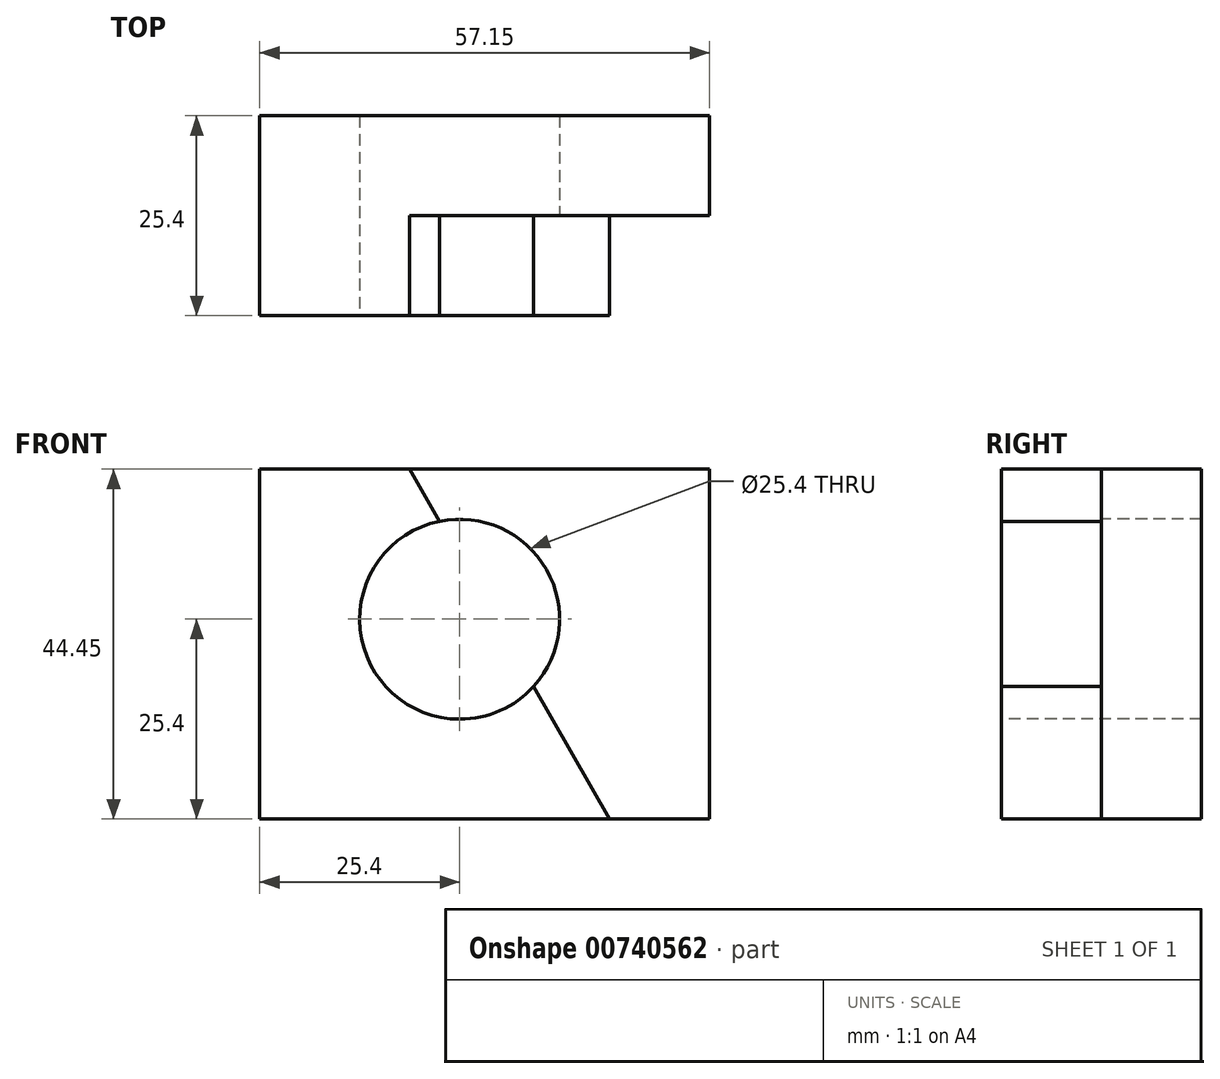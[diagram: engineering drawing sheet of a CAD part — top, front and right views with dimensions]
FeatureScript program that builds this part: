
annotation { "Feature Type Name" : "Feature", "Feature Type Description" : "" }
export const myFeature = defineFeature(function(context is Context, id is Id, definition is map)
    precondition{}
    {
        {
            var Q0;
            Q0=qCreatedBy(makeId("Front.planeOp"),FACE);
            var sketch = newSketch(context, id + "F0", { "sketchPlane" : qUnion([Q0])});
            skLineSegment(sketch, "E0.bottom", {"start": v(0, 0) * mm, "end": v(57.15, 0) * mm});
            skLineSegment(sketch, "E0.top", {"start": v(0, 44.45) * mm, "end": v(57.15, 44.45) * mm});
            skLineSegment(sketch, "E0.left", {"start": v(0, 0) * mm, "end": v(0, 44.45) * mm});
            skLineSegment(sketch, "E0.right", {"start": v(57.15, 0) * mm, "end": v(57.15, 44.45) * mm});
            skSolve(sketch);
        }
        {
            var Q0;
            Q0 = qSketchRegion(id + "F0", true);
            extrude(context, id + "F1", {"entities" : qUnion([Q0]), "depth" : 25.4 * mm, "offsetDistance" : 25.4 * mm});
        }
        {
            var Q0;
            Q0=makeQuery(id+"F1.opExtrude","CAP_FACE",FACE,{"disambiguationData":[OSD([sQuery(id+"F0.wireOp",EDGE,"E0.bottom"),sQuery(id+"F0.wireOp",EDGE,"E0.top"),sQuery(id+"F0.wireOp",EDGE,"E0.left"),sQuery(id+"F0.wireOp",EDGE,"E0.right")])],"isStart":false});
            var sketch = newSketch(context, id + "F2", { "sketchPlane" : qUnion([Q0])});
            skLineSegment(sketch, "E1", {"start": v(0, 25.4) * mm, "end": v(57.15, 25.4) * mm});
            skLineSegment(sketch, "E2", {"start": v(25.4, 44.45) * mm, "end": v(25.4, 0) * mm});
            skCircle(sketch, "E3", {"center": v(25.4, 25.4) * mm, "radius": 12.7 * mm});
            skPoint(sketch, "E3.centerSnap0", {"position": v(25.4, 22.22) * mm});
            skPoint(sketch, "E3.centerSnap1", {"position": v(28.58, 25.4) * mm});
            skSolve(sketch);
        }
        {
            var Q0;
            Q0 = qSketchRegion(id + "F2", true);
            extrude(context, id + "F3", {"entities" : qUnion([Q0]), "operationType" : NewBodyOperationType.REMOVE, "endBound" : BoundingType.THROUGH_ALL, "oppositeDirection" : true, "depth" : 25.4 * mm, "offsetDistance" : 25.4 * mm});
        }
        {
            var Q0;
            Q0=makeQuery(id+"F1.opExtrude","CAP_FACE",FACE,{"disambiguationData":[OSD([sQuery(id+"F0.wireOp",EDGE,"E0.bottom"),sQuery(id+"F0.wireOp",EDGE,"E0.top"),sQuery(id+"F0.wireOp",EDGE,"E0.left"),sQuery(id+"F0.wireOp",EDGE,"E0.right")])],"isStart":false});
            var sketch = newSketch(context, id + "F4", { "sketchPlane" : qUnion([Q0])});
            skLineSegment(sketch, "E4", {"start": v(19.05, 44.45) * mm, "end": v(44.45, 0) * mm});
            skSolve(sketch);
        }
        {
            var Q0;
            Q0 = qSketchRegion(id + "F4", true);
            var Q1;
            {var subQ0=makeQuery(id+"F1.opExtrude","CAP_EDGE",EDGE,{"disambiguationData":[OSD([sQuery(id+"F0.wireOp",EDGE,"E0.right")])],"isStart":false});Q1=makeQuery(id+"F4.imprint","IMPRINT",FACE,{"disambiguationData":[TD([[makeQuery(id+"F4.imprint","IMPRINT",EDGE,{"derivedFrom":subQ0}),1.0]])]});}
            extrude(context, id + "F5", {"entities" : qUnion([Q0, Q1]), "operationType" : NewBodyOperationType.REMOVE, "oppositeDirection" : true, "depth" : 12.7 * mm, "offsetDistance" : 25.4 * mm});
        }
    });
